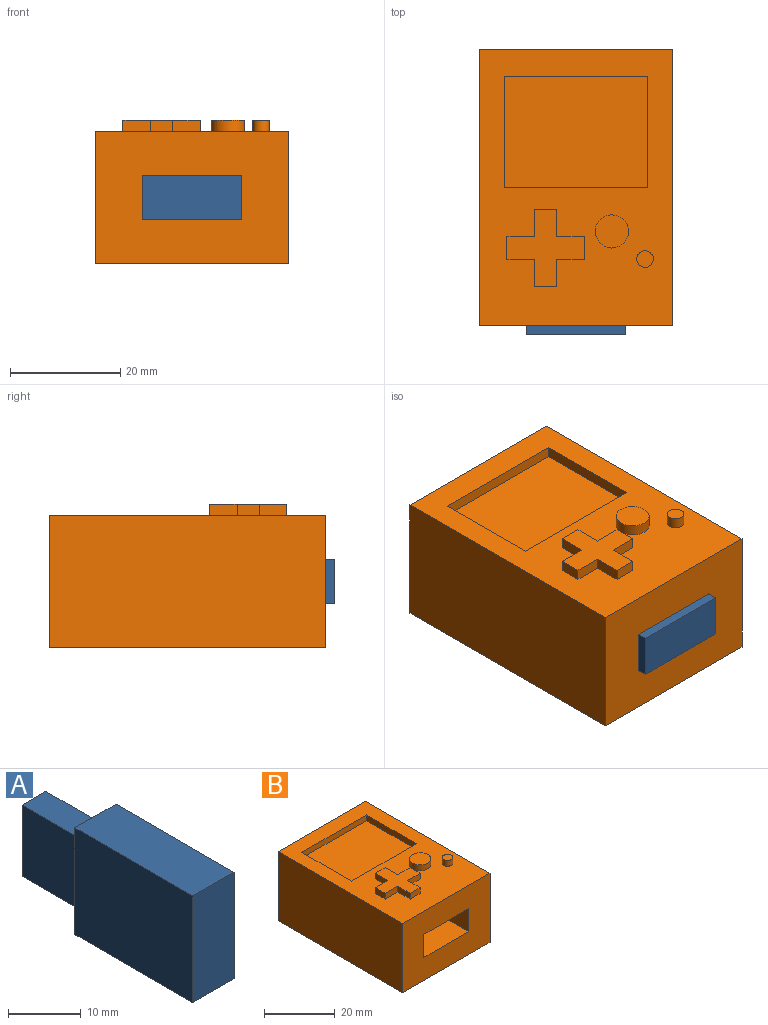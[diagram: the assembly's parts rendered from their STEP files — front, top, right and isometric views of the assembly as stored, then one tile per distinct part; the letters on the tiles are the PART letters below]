
ASSEMBLY  parts=2 mates=2
PART A: 11 faces, bbox 8x35x18 mm
  f0: plane 12x12mm, normal (-1,0,0), area 144mm2, adj f1,f3,f4,f5
  f1: plane 12x4.65mm, normal (0,0,-1), area 55.8mm2, adj f0,f2,f4,f5
  f2: plane 12x12mm, normal (1,0,0), area 144mm2, adj f1,f3,f4,f5
  f3: plane 12x4.65mm, normal (0,0,1), area 55.8mm2, adj f0,f2,f4,f5
  f4: plane 12x4.65mm, normal (0,1,0), area 55.8mm2, adj f0,f1,f2,f3
  f5: plane 18x8mm, normal (0,1,0), area 88.2mm2, adj f0,f1,f2,f3,f6,f7,f8,f9
  f6: plane 23x18mm, normal (-1,0,0), area 414mm2, adj f5,f7,f9,f10
  f7: plane 23x8mm, normal (0,0,1), area 184mm2, adj f5,f6,f8,f10
  f8: plane 23x18mm, normal (1,0,0), area 414mm2, adj f5,f7,f9,f10
  f9: plane 23x8mm, normal (0,0,-1), area 184mm2, adj f5,f6,f8,f10
  f10: plane 18x8mm, normal (0,-1,0), area 144mm2, adj f6,f7,f8,f9
PART B: 33 faces, bbox 35x50x26 mm
  f0: plane 50x24mm, normal (-1,0,0), area 1200mm2, adj f1,f3,f4,f5
  f1: plane 35x24mm, normal (0,-1,0), area 696mm2, adj f0,f2,f4,f5,f6,f7,f8,f9
  f2: plane 50x24mm, normal (1,0,0), area 1200mm2, adj f1,f3,f4,f5
  f3: plane 35x24mm, normal (0,1,0), area 840mm2, adj f0,f2,f4,f5
  f4: plane 50x35mm, normal (0,0,1), area 1098.7mm2, adj f0,f1,f2,f3,f11,f13,f15,f16
  f5: plane 50x35mm, normal (0,0,-1), area 1750mm2, adj f0,f1,f2,f3
  f6: plane 30x8mm, normal (-1,0,0), area 240mm2, adj f1,f7,f9,f10
  f7: plane 30x18mm, normal (0,0,1), area 540mm2, adj f1,f6,f8,f10
  f8: plane 30x8mm, normal (1,0,0), area 240mm2, adj f1,f7,f9,f10
  f9: plane 30x18mm, normal (0,0,-1), area 540mm2, adj f1,f6,f8,f10
  f10: plane 18x8mm, normal (0,-1,0), area 144mm2, adj f6,f7,f8,f9
  f11: cylinder r=3mm len=6mm, axis (0,0,-1), area 37.7mm2, adj f4,f12
  f12: plane 6x6mm, normal (0,0,1), area 28.3mm2, adj f11
  f13: cylinder r=1.5mm len=3mm, axis (0,0,-1), area 18.8mm2, adj f4,f14
  f14: plane 3x3mm, normal (0,0,1), area 7.1mm2, adj f13
  f15: plane 4x2mm, normal (-1,0,0), area 8mm2, adj f4,f16,f26,f27
  f16: plane 5x2mm, normal (0,-1,0), area 10mm2, adj f4,f15,f17,f27
  f17: plane 5x2mm, normal (-1,0,0), area 10mm2, adj f4,f16,f18,f27
  f18: plane 4x2mm, normal (0,-1,0), area 8mm2, adj f4,f17,f19,f27
  f19: plane 5x2mm, normal (1,0,0), area 10mm2, adj f4,f18,f20,f27
  f20: plane 5x2mm, normal (0,-1,0), area 10mm2, adj f4,f19,f21,f27
  f21: plane 4x2mm, normal (1,0,0), area 8mm2, adj f4,f20,f22,f27
  f22: plane 5x2mm, normal (0,1,0), area 10mm2, adj f4,f21,f23,f27
  f23: plane 5x2mm, normal (1,0,0), area 10mm2, adj f4,f22,f24,f27
  f24: plane 4x2mm, normal (0,1,0), area 8mm2, adj f4,f23,f25,f27
  f25: plane 5x2mm, normal (-1,0,0), area 10mm2, adj f4,f24,f26,f27
  f26: plane 5x2mm, normal (0,1,0), area 10mm2, adj f4,f15,f25,f27
  f27: plane 14x14mm, normal (0,0,1), area 96mm2, adj f15,f16,f17,f18,f19,f20,f21,f22
  f28: plane 20x2mm, normal (-1,0,0), area 40mm2, adj f4,f29,f31,f32
  f29: plane 26x2mm, normal (0,1,0), area 52mm2, adj f4,f28,f30,f32
  f30: plane 20x2mm, normal (1,0,0), area 40mm2, adj f4,f29,f31,f32
  f31: plane 26x2mm, normal (0,-1,0), area 52mm2, adj f4,f28,f30,f32
  f32: plane 26x20mm, normal (0,0,1), area 520mm2, adj f28,f29,f30,f31
PLACE A rot(axis=(0,1,0),90deg) t=(2.2,-6.1,1.73)mm
PLACE B t=(2.2,3.08,1.73)mm fixed
MATE planar A.f7 <-> B.f6  axis (1,0,0) through (11.2,-12.1,1.73)mm
MATE planar A.f8 <-> B.f7  axis (0,0,-1) through (2.2,-12.1,-2.27)mm
